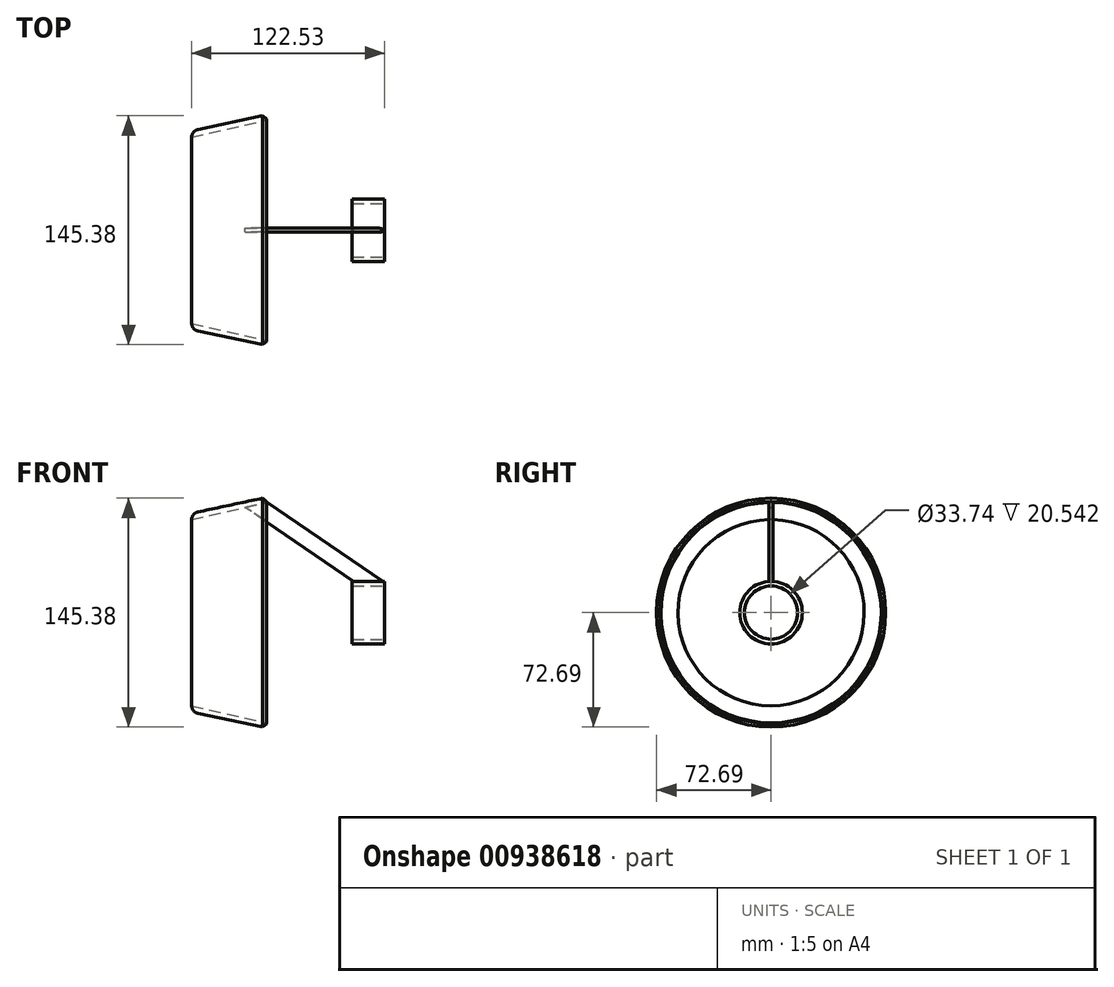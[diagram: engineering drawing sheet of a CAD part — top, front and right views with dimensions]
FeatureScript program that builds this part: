
annotation { "Feature Type Name" : "Feature", "Feature Type Description" : "" }
export const myFeature = defineFeature(function(context is Context, id is Id, definition is map)
    precondition{}
    {
        {
            var Q0;
            Q0=qCreatedBy(makeId("Front.planeOp"),FACE);
            var sketch = newSketch(context, id + "F0", { "sketchPlane" : qUnion([Q0])});
            skLineSegment(sketch, "E0", {"start": v(-76.23, 0) * mm, "end": v(75.6, 0) * mm});
            skSolve(sketch);
        }
        {
            var Q0;
            Q0=qCreatedBy(makeId("Top.planeOp"),FACE);
            var sketch = newSketch(context, id + "F1", { "sketchPlane" : qUnion([Q0])});
            skLineSegment(sketch, "E1", {"start": v(20.83, -70.33) * mm, "end": v(20.83, -73.46) * mm});
            skLineSegment(sketch, "E2", {"start": v(20.83, -73.46) * mm, "end": v(-27.9, -63.11) * mm});
            skLineSegment(sketch, "E3", {"start": v(-27.9, -63.11) * mm, "end": v(-27.9, -59.11) * mm});
            skLineSegment(sketch, "E4", {"start": v(-27.9, -59.11) * mm, "end": v(20.83, -70.33) * mm});
            skSolve(sketch);
        }
        {
            var Q0;
            Q0=makeQuery(id+"F1.imprint","IMPRINT",FACE,{"disambiguationData":[TD([[makeQuery(id+"F1.imprint","IMPRINT",EDGE,{"derivedFrom":sQuery(id+"F1.wireOp",EDGE,"E1")}),-1.0]])]});
            var Q1;
            Q1=sQuery(id+"F0.wireOp",EDGE,"E0");
            revolve(context, id + "F2", {"surfaceOperationType" : NewSurfaceOperationType.NEW, "entities" : qUnion([Q0]), "axis" : qUnion([Q1]), "revolveType" : RevolveType.FULL});
        }
        {
            var Q0;
            Q0=makeQuery(id+"F2.opRevolve","SWEPT_EDGE",EDGE,{"disambiguationData":[OSD([sQuery(id+"F1.wireOp",EDGE,"E2"),sQuery(id+"F1.wireOp",EDGE,"E3")])]});
            fillet(context, id + "F3", {"entities" : qUnion([Q0]), "radius" : 5 * mm, "tangentPropagation" : true, "allowEdgeOverflow" : false});
        }
        {
            var Q0;
            Q0=qCreatedBy(makeId("Front.planeOp"),FACE);
            var sketch = newSketch(context, id + "F4", { "sketchPlane" : qUnion([Q0])});
            skLineSegment(sketch, "E5.bottom", {"start": v(93.91, 19.65) * mm, "end": v(75.2, 19.65) * mm});
            skLineSegment(sketch, "E5.top", {"start": v(19.69, 70.48) * mm, "end": v(5.7, 67.25) * mm});
            skLineSegment(sketch, "E5.left", {"start": v(93.91, 19.65) * mm, "end": v(19.69, 70.48) * mm});
            skLineSegment(sketch, "E5.right", {"start": v(75.2, 19.65) * mm, "end": v(5.7, 67.25) * mm});
            skPoint(sketch, "E5.middle", {"position": v(53.29, 41.14) * mm});
            skSolve(sketch);
        }
        {
            var Q0;
            Q0=makeQuery(id+"F2.opRevolve","SWEPT_EDGE",EDGE,{"disambiguationData":[OSD([sQuery(id+"F1.wireOp",EDGE,"E1"),sQuery(id+"F1.wireOp",EDGE,"E4")])]});
            chamfer(context, id + "F5", {"entities" : qUnion([Q0]), "width" : 2 * mm, "tangentPropagation" : true});
        }
        {
            var Q0;
            Q0=makeQuery(id+"F4.imprint","IMPRINT",FACE,{"disambiguationData":[TD([[makeQuery(id+"F4.imprint","IMPRINT",EDGE,{"derivedFrom":sQuery(id+"F4.wireOp",EDGE,"E5.bottom")}),-1.0]])]});
            extrude(context, id + "F6", {"entities" : qUnion([Q0]), "operationType" : NewBodyOperationType.ADD, "depth" : 1.25 * mm, "offsetDistance" : 25 * mm, "hasSecondDirection" : true, "secondDirectionOppositeDirection" : true, "secondDirectionDepth" : 1.25 * mm});
        }
        {
            var Q0;
            Q0=makeQuery(id+"F6.opExtrude","CAP_EDGE",EDGE,{"disambiguationData":[OSD([sQuery(id+"F4.wireOp",EDGE,"E5.left")])],"isStart":false});
            var Q1;
            Q1=makeQuery(id+"F6.opExtrude","CAP_EDGE",EDGE,{"disambiguationData":[OSD([sQuery(id+"F4.wireOp",EDGE,"E5.left")])],"isStart":true});
            fillet(context, id + "F7", {"entities" : qUnion([Q0, Q1]), "radius" : 1.25 * mm, "tangentPropagation" : true, "allowEdgeOverflow" : false});
        }
        {
            var Q0;
            Q0=qCreatedBy(makeId("Front.planeOp"),FACE);
            var sketch = newSketch(context, id + "F8", { "sketchPlane" : qUnion([Q0])});
            skLineSegment(sketch, "E6.bottom", {"start": v(74.1, 19.87) * mm, "end": v(94.63, 19.87) * mm});
            skLineSegment(sketch, "E6.top", {"start": v(74.1, 16.87) * mm, "end": v(94.63, 16.87) * mm});
            skLineSegment(sketch, "E6.left", {"start": v(74.1, 19.87) * mm, "end": v(74.1, 16.87) * mm});
            skLineSegment(sketch, "E6.right", {"start": v(94.63, 19.87) * mm, "end": v(94.63, 16.87) * mm});
            skSolve(sketch);
        }
        {
            var Q0;
            Q0=makeQuery(id+"F8.imprint","IMPRINT",FACE,{"disambiguationData":[TD([[makeQuery(id+"F8.imprint","IMPRINT",EDGE,{"derivedFrom":sQuery(id+"F8.wireOp",EDGE,"E6.bottom")}),-1.0]])]});
            var Q1;
            Q1=makeQuery(id+"F2.opRevolve","SWEPT_EDGE",EDGE,{"disambiguationData":[OSD([sQuery(id+"F1.wireOp",EDGE,"E1"),sQuery(id+"F1.wireOp",EDGE,"E2")])]});
            revolve(context, id + "F9", {"operationType" : NewBodyOperationType.ADD, "surfaceOperationType" : NewSurfaceOperationType.NEW, "entities" : qUnion([Q0]), "axis" : qUnion([Q1]), "revolveType" : RevolveType.FULL});
        }
        {
            var Q0;
            Q0=makeQuery(id+"F2.opRevolve","SWEPT_EDGE",EDGE,{"disambiguationData":[OSD([sQuery(id+"F1.wireOp",EDGE,"E1"),sQuery(id+"F1.wireOp",EDGE,"E2")])]});
            chamfer(context, id + "F10", {"entities" : qUnion([Q0]), "width" : 3 * mm, "tangentPropagation" : true});
        }
    });
